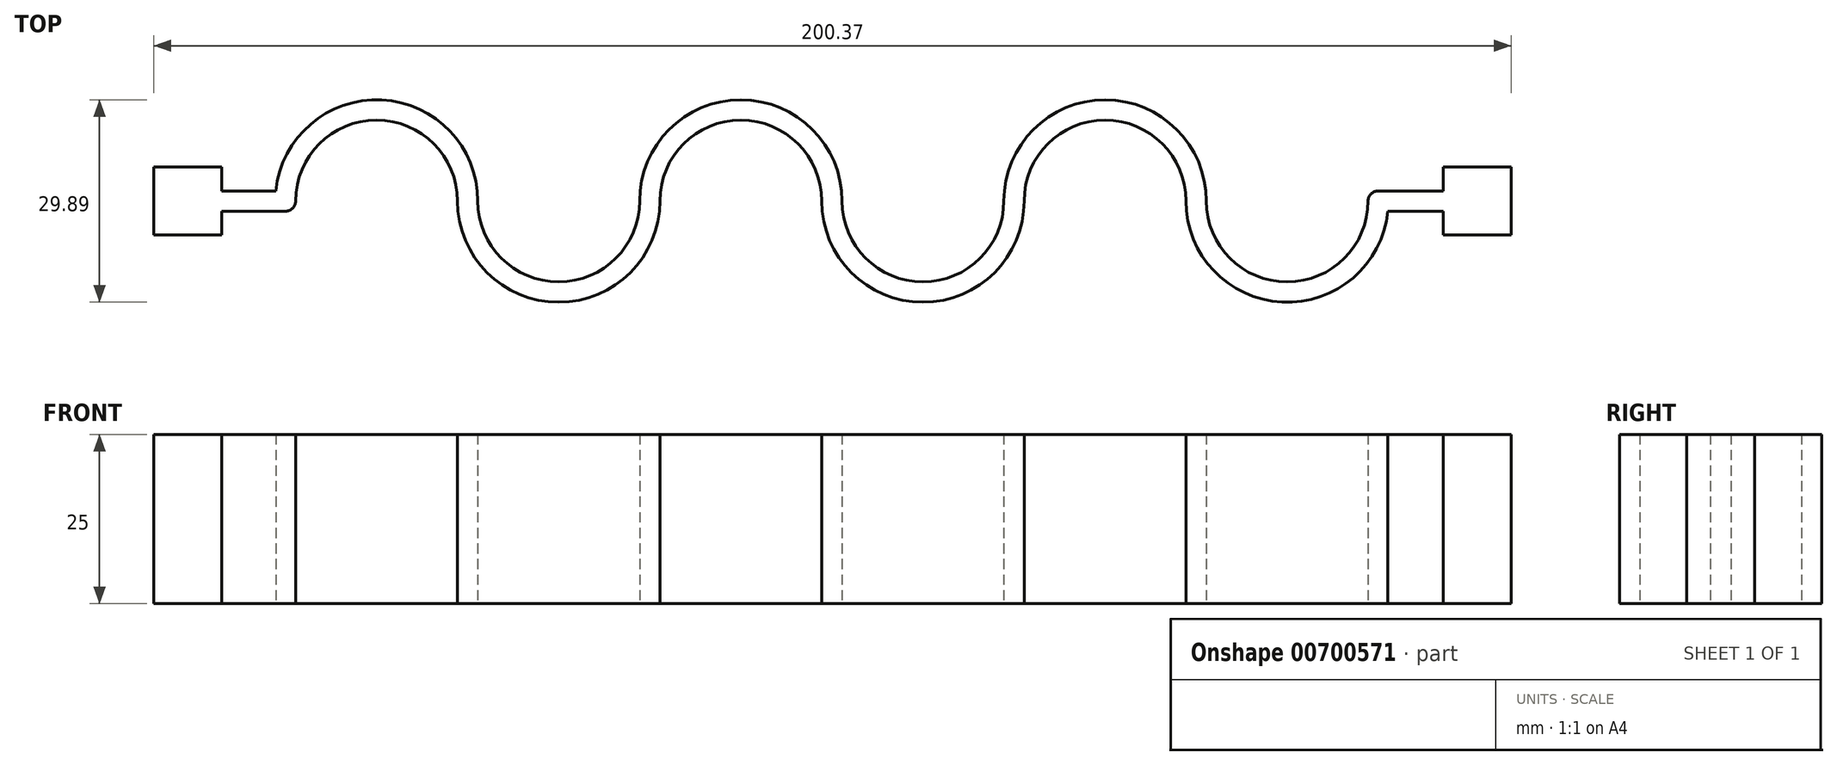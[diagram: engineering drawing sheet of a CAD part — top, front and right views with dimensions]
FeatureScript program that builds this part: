
annotation { "Feature Type Name" : "Feature", "Feature Type Description" : "" }
export const myFeature = defineFeature(function(context is Context, id is Id, definition is map)
    precondition{}
    {
        {
            var Q0;
            Q0=qCreatedBy(makeId("Top.planeOp"),FACE);
            var sketch = newSketch(context, id + "F0", { "sketchPlane" : qUnion([Q0])});
            skLineSegment(sketch, "E0", {"start": v(-57.17, 0.82) * mm, "end": v(-47.73, 0.82) * mm});
            skArc(sketch, "E1", {"start": v(-47.73, 0.82) * mm, "mid": v(-34.29, 14.26) * mm, "end": v(-20.84, 0.82) * mm});
            skArc(sketch, "E2.MirrorCS", {"start": v(6.04, 0.82) * mm, "mid": v(-7.4, -12.63) * mm, "end": v(-20.84, 0.82) * mm});
            skArc(sketch, "E3", {"start": v(6.04, 0.82) * mm, "mid": v(19.49, 14.26) * mm, "end": v(32.93, 0.82) * mm});
            skArc(sketch, "E4.MirrorCS", {"start": v(59.82, 0.82) * mm, "mid": v(46.37, -12.63) * mm, "end": v(32.93, 0.82) * mm});
            skArc(sketch, "E5", {"start": v(59.82, 0.82) * mm, "mid": v(73.26, 14.26) * mm, "end": v(86.7, 0.82) * mm});
            skArc(sketch, "E6.MirrorCS", {"start": v(113.6, 0.82) * mm, "mid": v(100.15, -12.63) * mm, "end": v(86.7, 0.82) * mm});
            skLineSegment(sketch, "E7.MirrorCS", {"start": v(123.2, 0.82) * mm, "end": v(113.6, 0.82) * mm});
            skArc(sketch, "E8.0.endCap", {"start": v(113.6, -0.68) * mm, "mid": v(112.1, 0.82) * mm, "end": v(113.6, 2.32) * mm});
            skLineSegment(sketch, "E8.0.left", {"start": v(123.2, -0.68) * mm, "end": v(113.6, -0.68) * mm});
            skLineSegment(sketch, "E8.0.right", {"start": v(123.2, 2.32) * mm, "end": v(113.6, 2.32) * mm});
            skArc(sketch, "E8.1.startCap", {"start": v(7.54, 0.82) * mm, "mid": v(6.04, -0.68) * mm, "end": v(4.54, 0.82) * mm});
            skArc(sketch, "E8.1.endCap", {"start": v(34.43, 0.82) * mm, "mid": v(32.93, -0.68) * mm, "end": v(31.43, 0.82) * mm});
            skArc(sketch, "E8.1.left", {"start": v(4.54, 0.82) * mm, "mid": v(19.49, 15.76) * mm, "end": v(34.43, 0.82) * mm});
            skArc(sketch, "E8.1.right", {"start": v(7.54, 0.82) * mm, "mid": v(19.49, 12.76) * mm, "end": v(31.43, 0.82) * mm});
            skArc(sketch, "E8.2.startCap", {"start": v(61.32, 0.82) * mm, "mid": v(59.82, -0.68) * mm, "end": v(58.32, 0.82) * mm});
            skArc(sketch, "E8.2.endCap", {"start": v(88.2, 0.82) * mm, "mid": v(86.7, -0.68) * mm, "end": v(85.2, 0.82) * mm});
            skArc(sketch, "E8.2.left", {"start": v(58.32, 0.82) * mm, "mid": v(73.26, 15.76) * mm, "end": v(88.2, 0.82) * mm});
            skArc(sketch, "E8.2.right", {"start": v(61.32, 0.82) * mm, "mid": v(73.26, 12.76) * mm, "end": v(85.2, 0.82) * mm});
            skArc(sketch, "E8.3.endCap", {"start": v(-47.73, 2.32) * mm, "mid": v(-46.23, 0.82) * mm, "end": v(-47.73, -0.68) * mm});
            skLineSegment(sketch, "E8.3.left", {"start": v(-57.17, 2.32) * mm, "end": v(-47.73, 2.32) * mm});
            skLineSegment(sketch, "E8.3.right", {"start": v(-57.17, -0.68) * mm, "end": v(-47.73, -0.68) * mm});
            skArc(sketch, "E8.4.startCap", {"start": v(58.32, 0.82) * mm, "mid": v(59.82, 2.32) * mm, "end": v(61.32, 0.82) * mm});
            skArc(sketch, "E8.4.endCap", {"start": v(31.43, 0.82) * mm, "mid": v(32.93, 2.32) * mm, "end": v(34.43, 0.82) * mm});
            skArc(sketch, "E8.4.left", {"start": v(61.32, 0.82) * mm, "mid": v(46.37, -14.13) * mm, "end": v(31.43, 0.82) * mm});
            skArc(sketch, "E8.4.right", {"start": v(58.32, 0.82) * mm, "mid": v(46.37, -11.13) * mm, "end": v(34.43, 0.82) * mm});
            skArc(sketch, "E8.5.startCap", {"start": v(-46.23, 0.82) * mm, "mid": v(-47.73, -0.68) * mm, "end": v(-49.23, 0.82) * mm});
            skArc(sketch, "E8.5.endCap", {"start": v(-19.34, 0.82) * mm, "mid": v(-20.84, -0.68) * mm, "end": v(-22.34, 0.82) * mm});
            skArc(sketch, "E8.5.left", {"start": v(-49.23, 0.82) * mm, "mid": v(-34.29, 15.76) * mm, "end": v(-19.34, 0.82) * mm});
            skArc(sketch, "E8.5.right", {"start": v(-46.23, 0.82) * mm, "mid": v(-34.29, 12.76) * mm, "end": v(-22.34, 0.82) * mm});
            skArc(sketch, "E8.6.startCap", {"start": v(112.1, 0.82) * mm, "mid": v(113.6, 2.32) * mm, "end": v(115.1, 0.82) * mm});
            skArc(sketch, "E8.6.endCap", {"start": v(85.2, 0.82) * mm, "mid": v(86.7, 2.32) * mm, "end": v(88.2, 0.82) * mm});
            skArc(sketch, "E8.6.left", {"start": v(115.1, 0.82) * mm, "mid": v(100.15, -14.13) * mm, "end": v(85.2, 0.82) * mm});
            skArc(sketch, "E8.6.right", {"start": v(112.1, 0.82) * mm, "mid": v(100.15, -11.13) * mm, "end": v(88.2, 0.82) * mm});
            skArc(sketch, "E8.7.startCap", {"start": v(4.54, 0.82) * mm, "mid": v(6.04, 2.32) * mm, "end": v(7.54, 0.82) * mm});
            skArc(sketch, "E8.7.endCap", {"start": v(-22.34, 0.82) * mm, "mid": v(-20.84, 2.32) * mm, "end": v(-19.34, 0.82) * mm});
            skArc(sketch, "E8.7.left", {"start": v(7.54, 0.82) * mm, "mid": v(-7.4, -14.13) * mm, "end": v(-22.34, 0.82) * mm});
            skArc(sketch, "E8.7.right", {"start": v(4.54, 0.82) * mm, "mid": v(-7.4, -11.13) * mm, "end": v(-19.34, 0.82) * mm});
            skLineSegment(sketch, "E9.bottom", {"start": v(133.2, -4.18) * mm, "end": v(123.2, -4.18) * mm});
            skLineSegment(sketch, "E9.top", {"start": v(133.2, 5.82) * mm, "end": v(123.2, 5.82) * mm});
            skLineSegment(sketch, "E9.left", {"start": v(133.2, -4.18) * mm, "end": v(133.2, 5.82) * mm});
            skLineSegment(sketch, "E9.right", {"start": v(123.2, -4.18) * mm, "end": v(123.2, 5.82) * mm});
            skPoint(sketch, "E9.middle", {"position": v(128.2, 0.82) * mm});
            skPoint(sketch, "E10.orphan", {"position": v(123.5, 0.82) * mm});
            skLineSegment(sketch, "E11.bottom", {"start": v(-57.17, 5.82) * mm, "end": v(-67.17, 5.82) * mm});
            skLineSegment(sketch, "E11.top", {"start": v(-57.17, -4.18) * mm, "end": v(-67.17, -4.18) * mm});
            skLineSegment(sketch, "E11.left", {"start": v(-57.17, 5.82) * mm, "end": v(-57.17, 2.32) * mm});
            skLineSegment(sketch, "E11.right", {"start": v(-67.17, 5.82) * mm, "end": v(-67.17, -4.18) * mm});
            skPoint(sketch, "E11.middle", {"position": v(-62.17, 0.82) * mm});
            skPoint(sketch, "E12.orphan", {"position": v(-57.64, 0.82) * mm});
            skLineSegment(sketch, "E13.trimOffspring", {"start": v(-57.17, -0.68) * mm, "end": v(-57.17, -4.18) * mm});
            skSolve(sketch);
        }
        {
            var Q0;
            Q0 = qSketchRegion(id + "F0", true);
            extrude(context, id + "F1", {"entities" : qUnion([Q0]), "depth" : 25 * mm, "offsetDistance" : 25 * mm});
        }
    });
